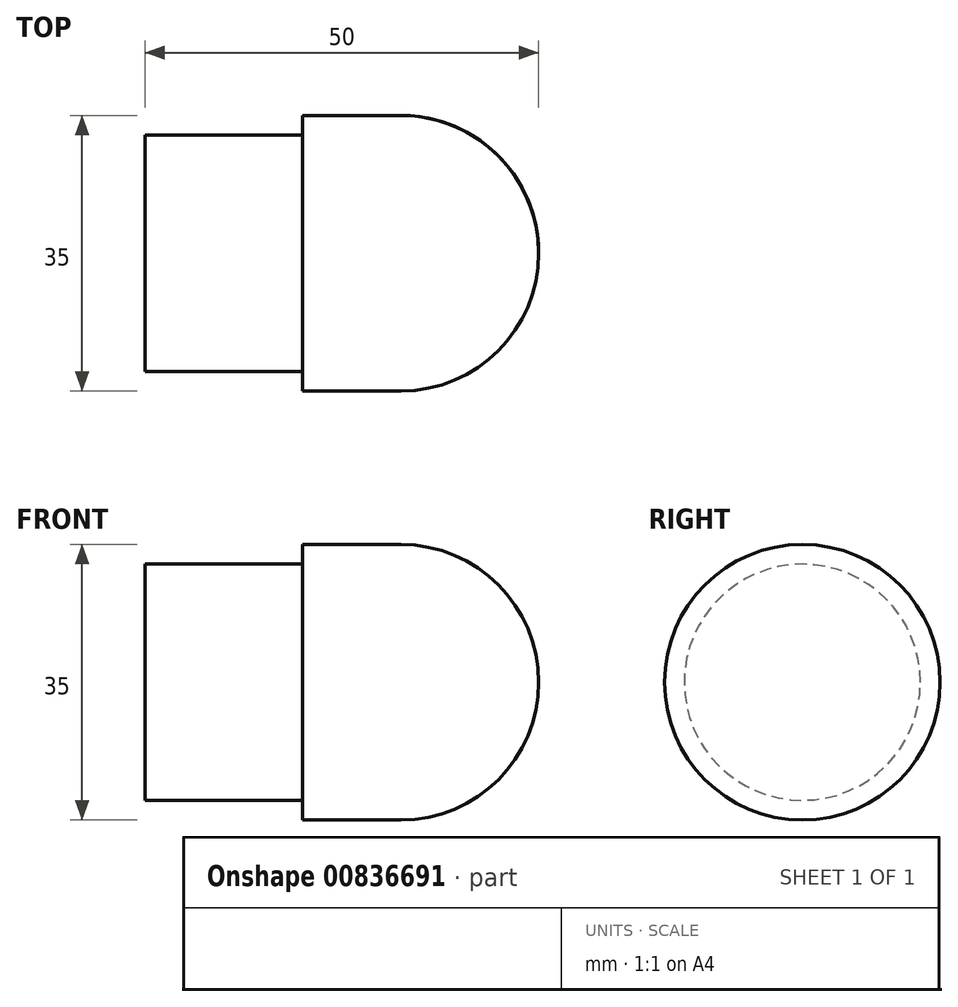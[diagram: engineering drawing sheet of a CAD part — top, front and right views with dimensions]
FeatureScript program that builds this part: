
annotation { "Feature Type Name" : "Feature", "Feature Type Description" : "" }
export const myFeature = defineFeature(function(context is Context, id is Id, definition is map)
    precondition{}
    {
        {
            var Q0;
            Q0=qCreatedBy(makeId("Top.planeOp"),FACE);
            var sketch = newSketch(context, id + "F0", { "sketchPlane" : qUnion([Q0])});
            skLineSegment(sketch, "E0", {"start": v(-32.5, 0) * mm, "end": v(0, 0) * mm});
            skLineSegment(sketch, "E1", {"start": v(0, 17.5) * mm, "end": v(-12.5, 17.5) * mm});
            skLineSegment(sketch, "E2", {"start": v(-12.5, 17.5) * mm, "end": v(-12.5, 15) * mm});
            skLineSegment(sketch, "E3", {"start": v(-12.5, 15) * mm, "end": v(-32.5, 15) * mm});
            skLineSegment(sketch, "E4", {"start": v(-32.5, 15) * mm, "end": v(-32.5, 0) * mm});
            skArc(sketch, "E5", {"start": v(17.5, 0) * mm, "mid": v(12.37, 12.37) * mm, "end": v(0, 17.5) * mm});
            skLineSegment(sketch, "E6", {"start": v(17.5, 0) * mm, "end": v(-32.5, 0) * mm});
            skSolve(sketch);
        }
        {
            var Q0;
            Q0=makeQuery(id+"F0.imprint","IMPRINT",FACE,{"disambiguationData":[TD([[makeQuery(id+"F0.imprint","IMPRINT",EDGE,{"derivedFrom":sQuery(id+"F0.wireOp",EDGE,"E1")}),1.0]])]});
            var Q1;
            Q1=sQuery(id+"F0.wireOp",EDGE,"E0");
            revolve(context, id + "F1", {"surfaceOperationType" : NewSurfaceOperationType.NEW, "entities" : qUnion([Q0]), "axis" : qUnion([Q1]), "revolveType" : RevolveType.FULL});
        }
    });
